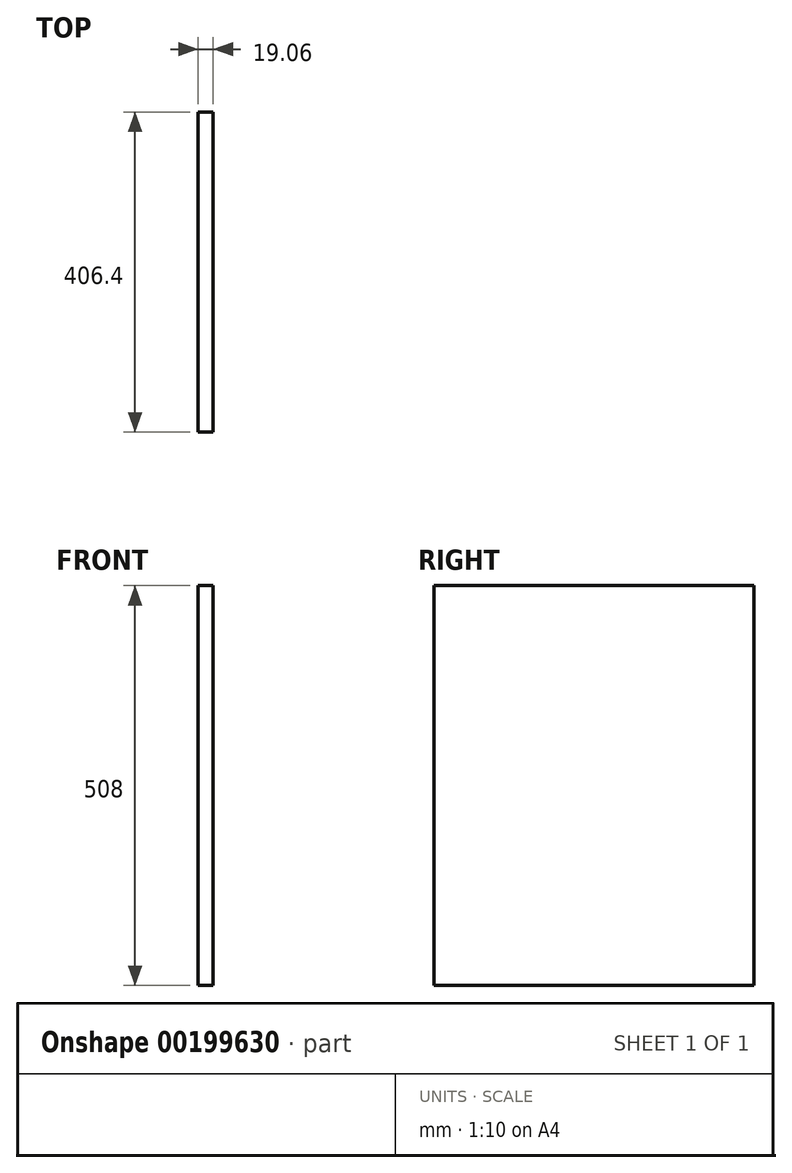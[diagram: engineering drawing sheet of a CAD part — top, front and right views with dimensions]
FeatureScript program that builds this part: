
annotation { "Feature Type Name" : "Feature", "Feature Type Description" : "" }
export const myFeature = defineFeature(function(context is Context, id is Id, definition is map)
    precondition{}
    {
        {
            var Q0;
            Q0=qCreatedBy(makeId("Right.planeOp"),FACE);
            var sketch = newSketch(context, id + "F0", { "sketchPlane" : qUnion([Q0])});
            skLineSegment(sketch, "E0.bottom", {"start": v(223.2, 170.58) * mm, "end": v(-183.2, 170.58) * mm});
            skLineSegment(sketch, "E0.top", {"start": v(223.2, -337.42) * mm, "end": v(-183.2, -337.42) * mm});
            skLineSegment(sketch, "E0.left", {"start": v(223.2, 170.58) * mm, "end": v(223.2, -337.42) * mm});
            skLineSegment(sketch, "E0.right", {"start": v(-183.2, 170.58) * mm, "end": v(-183.2, -337.42) * mm});
            skSolve(sketch);
        }
        {
            var Q0;
            Q0=makeQuery(id+"F0.imprint","IMPRINT",FACE,{"disambiguationData":[TD([[makeQuery(id+"F0.imprint","IMPRINT",EDGE,{"derivedFrom":sQuery(id+"F0.wireOp",EDGE,"E0.bottom")}),1.0]])]});
            extrude(context, id + "F1", {"entities" : qUnion([Q0]), "endBound" : BoundingType.SYMMETRIC, "depth" : 19.05 * mm});
        }
    });
